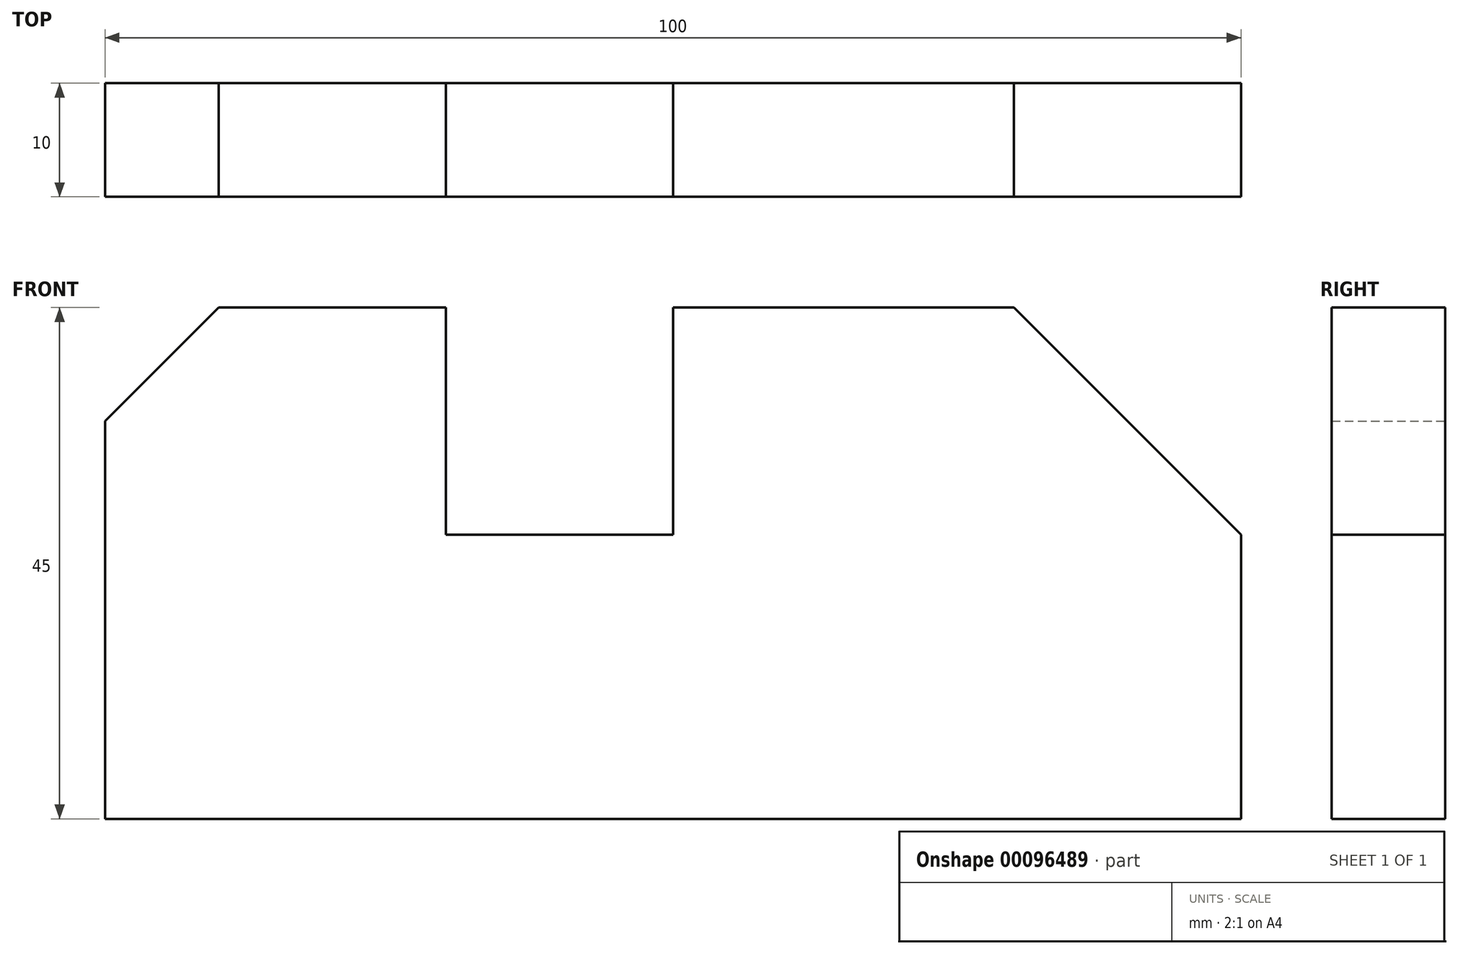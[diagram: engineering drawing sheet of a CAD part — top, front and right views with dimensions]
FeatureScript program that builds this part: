
annotation { "Feature Type Name" : "Feature", "Feature Type Description" : "" }
export const myFeature = defineFeature(function(context is Context, id is Id, definition is map)
    precondition{}
    {
        {
            var Q0;
            Q0=qCreatedBy(makeId("Front.planeOp"),FACE);
            var sketch = newSketch(context, id + "F0", { "sketchPlane" : qUnion([Q0])});
            skLineSegment(sketch, "E0.bottom", {"start": v(0, 0) * mm, "end": v(100, 0) * mm, "construction": true});
            skLineSegment(sketch, "E0.top", {"start": v(0, 45) * mm, "end": v(100, 45) * mm, "construction": true});
            skLineSegment(sketch, "E0.left", {"start": v(0, 0) * mm, "end": v(0, 45) * mm, "construction": true});
            skLineSegment(sketch, "E0.right", {"start": v(100, 0) * mm, "end": v(100, 45) * mm, "construction": true});
            skLineSegment(sketch, "E1", {"start": v(0, 0) * mm, "end": v(100, 0) * mm});
            skLineSegment(sketch, "E2", {"start": v(100, 0) * mm, "end": v(100, 25) * mm});
            skLineSegment(sketch, "E3", {"start": v(100, 25) * mm, "end": v(80, 45) * mm});
            skLineSegment(sketch, "E4", {"start": v(80, 45) * mm, "end": v(50, 45) * mm});
            skLineSegment(sketch, "E5", {"start": v(50, 45) * mm, "end": v(50, 25) * mm});
            skLineSegment(sketch, "E6", {"start": v(50, 25) * mm, "end": v(30, 25) * mm});
            skLineSegment(sketch, "E7", {"start": v(30, 25) * mm, "end": v(30, 45) * mm});
            skLineSegment(sketch, "E8", {"start": v(30, 45) * mm, "end": v(10, 45) * mm});
            skLineSegment(sketch, "E9", {"start": v(10, 45) * mm, "end": v(0, 35) * mm});
            skLineSegment(sketch, "E10", {"start": v(0, 35) * mm, "end": v(0, 0) * mm});
            skSolve(sketch);
        }
        {
            var Q0;
            Q0=makeQuery(id+"F0.imprint","IMPRINT",FACE,{"disambiguationData":[TD([[makeQuery(id+"F0.imprint","IMPRINT",EDGE,{"derivedFrom":sQuery(id+"F0.wireOp",EDGE,"E1")}),1.0]])]});
            extrude(context, id + "F1", {"entities" : qUnion([Q0]), "depth" : 10 * mm});
        }
    });
